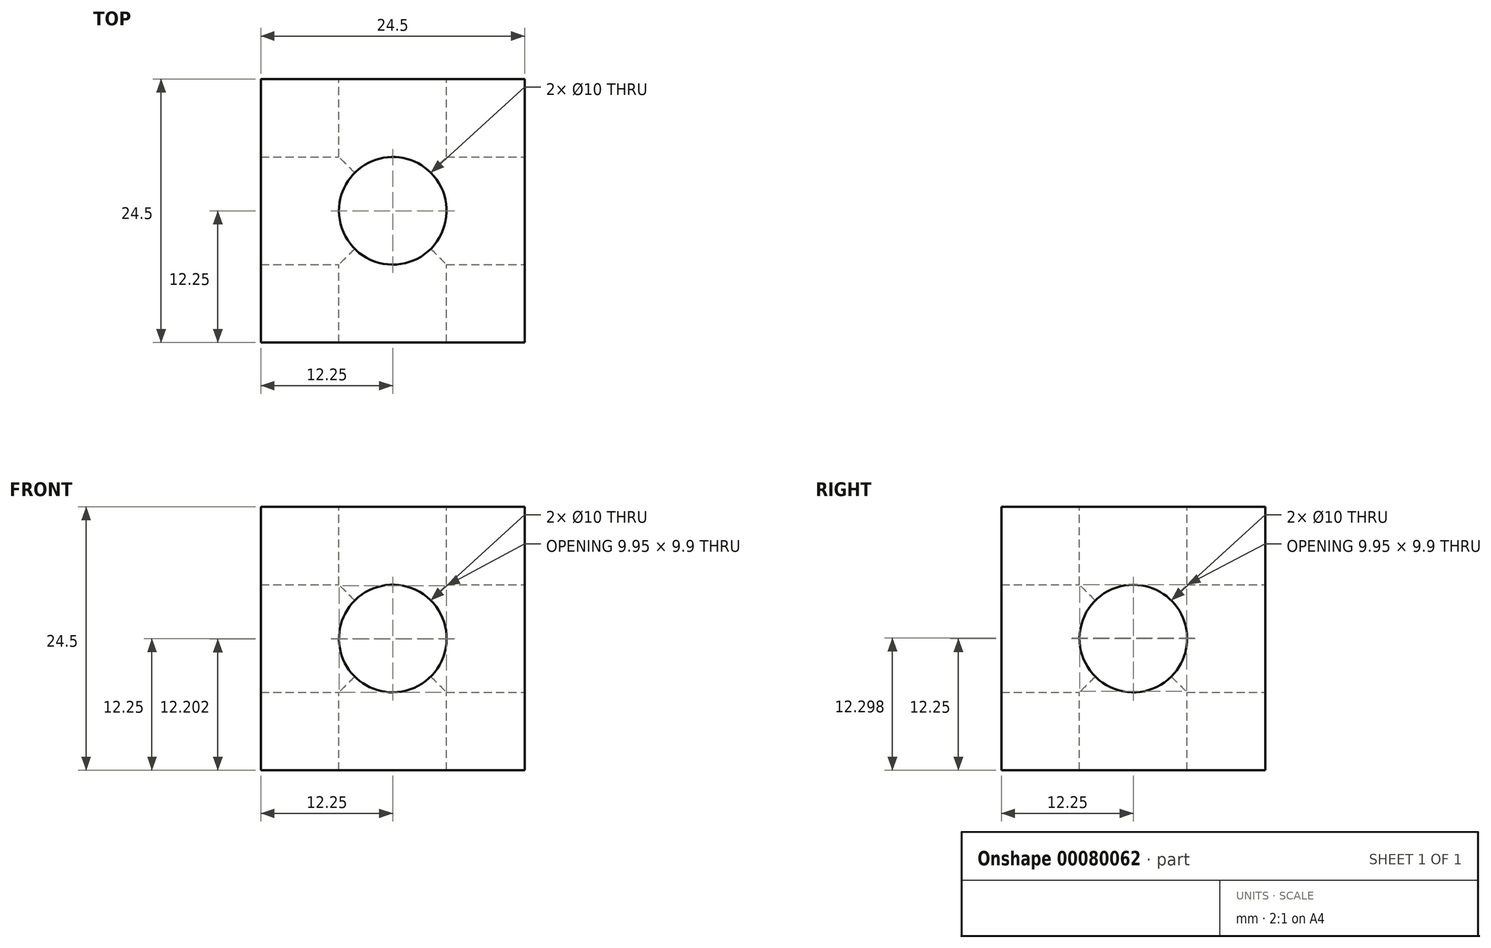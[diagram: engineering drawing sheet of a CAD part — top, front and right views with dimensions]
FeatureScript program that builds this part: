
annotation { "Feature Type Name" : "Feature", "Feature Type Description" : "" }
export const myFeature = defineFeature(function(context is Context, id is Id, definition is map)
    precondition{}
    {
        {
            var Q0;
            Q0=qCreatedBy(makeId("Front.planeOp"),FACE);
            var sketch = newSketch(context, id + "F0", { "sketchPlane" : qUnion([Q0])});
            skLineSegment(sketch, "E0.bottom", {"start": v(12.25, -12.25) * mm, "end": v(-12.25, -12.25) * mm});
            skLineSegment(sketch, "E0.top", {"start": v(12.25, 12.25) * mm, "end": v(-12.25, 12.25) * mm});
            skLineSegment(sketch, "E0.left", {"start": v(12.25, -12.25) * mm, "end": v(12.25, 12.25) * mm});
            skLineSegment(sketch, "E0.right", {"start": v(-12.25, -12.25) * mm, "end": v(-12.25, 12.25) * mm});
            skPoint(sketch, "E0.middle", {"position": v(0, 0) * mm});
            skCircle(sketch, "E1", {"center": v(0, 0) * mm, "radius": 5 * mm});
            skSolve(sketch);
        }
        {
            var Q0;
            Q0 = qSketchRegion(id + "F0", true);
            extrude(context, id + "F1", {"entities" : qUnion([Q0]), "endBound" : BoundingType.SYMMETRIC, "depth" : 24.5 * mm});
        }
        {
            var Q0;
            Q0=qCreatedBy(makeId("Right.planeOp"),FACE);
            var sketch = newSketch(context, id + "F2", { "sketchPlane" : qUnion([Q0])});
            skCircle(sketch, "E2", {"center": v(0, 0) * mm, "radius": 5 * mm});
            skSolve(sketch);
        }
        {
            var Q0;
            Q0 = qSketchRegion(id + "F2", true);
            extrude(context, id + "F3", {"entities" : qUnion([Q0]), "operationType" : NewBodyOperationType.REMOVE, "endBound" : BoundingType.THROUGH_ALL, "oppositeDirection" : true, "depth" : 25 * mm, "hasSecondDirection" : true, "secondDirectionBound" : SecondDirectionBoundingType.THROUGH_ALL, "secondDirectionOppositeDirection" : false, "secondDirectionDepth" : 25 * mm});
        }
        {
            var Q0;
            Q0=qCreatedBy(makeId("Top.planeOp"),FACE);
            var sketch = newSketch(context, id + "F4", { "sketchPlane" : qUnion([Q0])});
            skCircle(sketch, "E3", {"center": v(0, 0) * mm, "radius": 5 * mm});
            skSolve(sketch);
        }
        {
            var Q0;
            Q0 = qSketchRegion(id + "F4", true);
            extrude(context, id + "F5", {"entities" : qUnion([Q0]), "operationType" : NewBodyOperationType.REMOVE, "endBound" : BoundingType.THROUGH_ALL, "oppositeDirection" : true, "depth" : 25 * mm, "hasSecondDirection" : true, "secondDirectionBound" : SecondDirectionBoundingType.THROUGH_ALL, "secondDirectionOppositeDirection" : false, "secondDirectionDepth" : 25 * mm});
        }
    });
